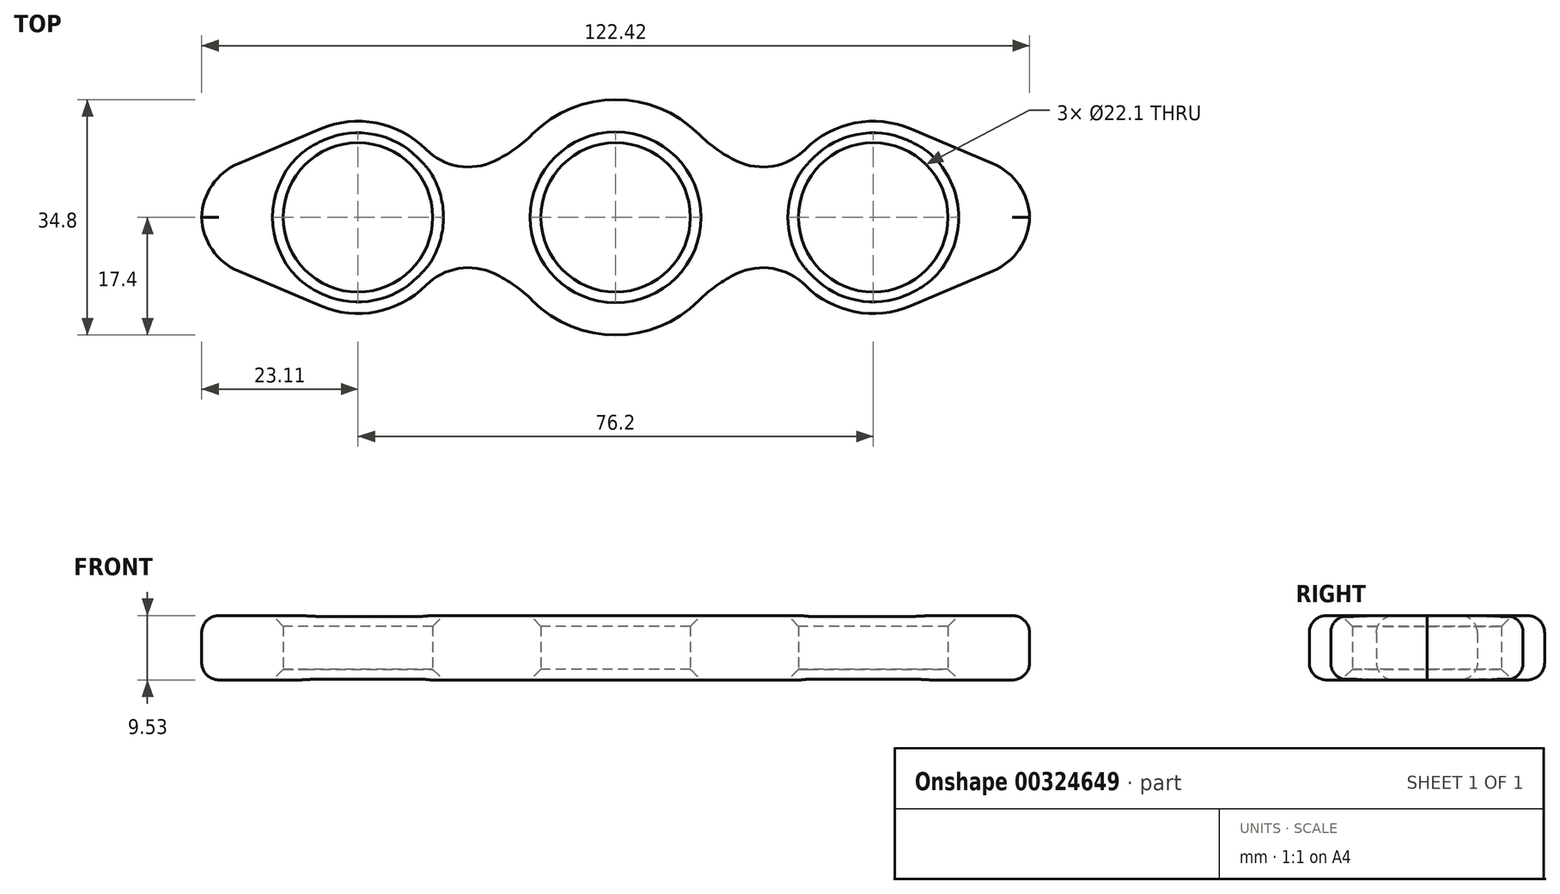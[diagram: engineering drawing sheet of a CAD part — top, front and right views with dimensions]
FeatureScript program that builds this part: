
annotation { "Feature Type Name" : "Feature", "Feature Type Description" : "" }
export const myFeature = defineFeature(function(context is Context, id is Id, definition is map)
    precondition{}
    {
        {
            var Q0;
            Q0=qCreatedBy(makeId("Top.planeOp"),FACE);
            var sketch = newSketch(context, id + "F0", { "sketchPlane" : qUnion([Q0])});
            skArc(sketch, "E0", {"start": v(0, 11.05) * mm, "mid": v(-7.81, 7.81) * mm, "end": v(-11.05, 0) * mm});
            skArc(sketch, "E1", {"start": v(-27.05, 0) * mm, "mid": v(-38.1, 11.05) * mm, "end": v(-49.15, 0) * mm});
            skArc(sketch, "E2", {"start": v(0, 17.4) * mm, "mid": v(-6.66, 16.07) * mm, "end": v(-12.3, 12.3) * mm});
            skArc(sketch, "E3", {"start": v(-28.04, 10.06) * mm, "mid": v(-35.39, 13.96) * mm, "end": v(-43.66, 13.1) * mm});
            skLineSegment(sketch, "E4", {"start": v(-43.66, 13.1) * mm, "end": v(-55.8, 7.94) * mm});
            skArc(sketch, "E5", {"start": v(-55.8, 7.94) * mm, "mid": v(-59.67, 4.77) * mm, "end": v(-61.2, 0) * mm});
            skPoint(sketch, "E6", {"position": v(0, 17.4) * mm});
            skArc(sketch, "E7", {"start": v(-17.9, 8.33) * mm, "mid": v(-14.94, 10.08) * mm, "end": v(-12.3, 12.3) * mm});
            skArc(sketch, "E8", {"start": v(-28.04, 10.06) * mm, "mid": v(-23.25, 7.58) * mm, "end": v(-17.9, 8.33) * mm});
            skLineSegment(sketch, "E9", {"start": v(0, 0) * mm, "end": v(-12.3, 12.3) * mm, "construction": true});
            skLineSegment(sketch, "E10", {"start": v(-38.1, 0) * mm, "end": v(-28.04, 10.06) * mm, "construction": true});
            skLineSegment(sketch, "E11", {"start": v(0, 17.4) * mm, "end": v(0, 0) * mm, "construction": true});
            skLineSegment(sketch, "E12", {"start": v(0, 0) * mm, "end": v(-61.2, 0) * mm, "construction": true});
            skPoint(sketch, "E13.center.orphan", {"position": v(38.1, 0) * mm});
            skPoint(sketch, "E14.end.orphan", {"position": v(-43.66, -13.1) * mm});
            skPoint(sketch, "E15.orphan", {"position": v(-55.8, -8.43) * mm});
            skArc(sketch, "E16.trimOffspring", {"start": v(-52.32, 0) * mm, "mid": v(-52.32, -0.12) * mm, "end": v(-52.32, -0.24) * mm});
            skArc(sketch, "E17.MirrorCS", {"start": v(-17.9, -8.33) * mm, "mid": v(-14.94, -10.08) * mm, "end": v(-12.3, -12.3) * mm});
            skArc(sketch, "E18.MirrorCS", {"start": v(-52.32, 0) * mm, "mid": v(-52.32, 0.12) * mm, "end": v(-52.32, 0.24) * mm});
            skLineSegment(sketch, "E19.MirrorCS", {"start": v(-43.66, -13.1) * mm, "end": v(-55.8, -7.94) * mm});
            skArc(sketch, "E20.MirrorCS", {"start": v(-55.8, -7.94) * mm, "mid": v(-59.67, -4.77) * mm, "end": v(-61.2, 0) * mm});
            skArc(sketch, "E21.MirrorCS", {"start": v(-28.04, -10.06) * mm, "mid": v(-23.25, -7.58) * mm, "end": v(-17.9, -8.33) * mm});
            skPoint(sketch, "E22.MirrorP", {"position": v(0, -17.4) * mm});
            skLineSegment(sketch, "E23.MirrorCS", {"start": v(0, 0) * mm, "end": v(-12.3, -12.3) * mm, "construction": true});
            skLineSegment(sketch, "E24.MirrorCS", {"start": v(0, -17.4) * mm, "end": v(0, 0) * mm, "construction": true});
            skArc(sketch, "E25.MirrorCS", {"start": v(-28.04, -10.06) * mm, "mid": v(-35.39, -13.96) * mm, "end": v(-43.66, -13.1) * mm});
            skArc(sketch, "E26.MirrorCS", {"start": v(-27.05, 0) * mm, "mid": v(-38.1, -11.05) * mm, "end": v(-49.15, 0) * mm});
            skArc(sketch, "E27.MirrorCS", {"start": v(0, -11.05) * mm, "mid": v(-7.81, -7.81) * mm, "end": v(-11.05, 0) * mm});
            skArc(sketch, "E28.MirrorCS", {"start": v(0, -17.4) * mm, "mid": v(-6.66, -16.07) * mm, "end": v(-12.3, -12.3) * mm});
            skLineSegment(sketch, "E29.MirrorCS", {"start": v(-38.1, 0) * mm, "end": v(-28.04, -10.06) * mm, "construction": true});
            skPoint(sketch, "E30.MirrorP", {"position": v(-55.8, 8.43) * mm});
            skArc(sketch, "E31.MirrorCS", {"start": v(52.32, 0) * mm, "mid": v(52.32, -0.12) * mm, "end": v(52.32, -0.24) * mm});
            skArc(sketch, "E32.MirrorCS", {"start": v(52.32, 0) * mm, "mid": v(52.32, 0.12) * mm, "end": v(52.32, 0.24) * mm});
            skArc(sketch, "E33.MirrorCS", {"start": v(17.9, 8.33) * mm, "mid": v(14.94, 10.08) * mm, "end": v(12.3, 12.3) * mm});
            skArc(sketch, "E34.MirrorCS", {"start": v(17.9, -8.33) * mm, "mid": v(14.94, -10.08) * mm, "end": v(12.3, -12.3) * mm});
            skPoint(sketch, "E35.MirrorP", {"position": v(55.8, 8.43) * mm});
            skArc(sketch, "E36.MirrorCS", {"start": v(55.8, -7.94) * mm, "mid": v(59.67, -4.77) * mm, "end": v(61.2, 0) * mm});
            skLineSegment(sketch, "E37.MirrorCS", {"start": v(0, 0) * mm, "end": v(12.3, -12.3) * mm, "construction": true});
            skPoint(sketch, "E38.MirrorP", {"position": v(43.66, -13.1) * mm});
            skArc(sketch, "E39.MirrorCS", {"start": v(28.04, -10.06) * mm, "mid": v(35.39, -13.96) * mm, "end": v(43.66, -13.1) * mm});
            skArc(sketch, "E40.MirrorCS", {"start": v(0, -11.05) * mm, "mid": v(7.81, -7.81) * mm, "end": v(11.05, 0) * mm});
            skArc(sketch, "E41.MirrorCS", {"start": v(0, -17.4) * mm, "mid": v(6.66, -16.07) * mm, "end": v(12.3, -12.3) * mm});
            skLineSegment(sketch, "E42.MirrorCS", {"start": v(0, 0) * mm, "end": v(61.2, 0) * mm, "construction": true});
            skLineSegment(sketch, "E43.MirrorCS", {"start": v(38.1, 0) * mm, "end": v(28.04, 10.06) * mm, "construction": true});
            skLineSegment(sketch, "E44.MirrorCS", {"start": v(0, 0) * mm, "end": v(12.3, 12.3) * mm, "construction": true});
            skArc(sketch, "E45.MirrorCS", {"start": v(28.04, 10.06) * mm, "mid": v(23.25, 7.58) * mm, "end": v(17.9, 8.33) * mm});
            skArc(sketch, "E46.MirrorCS", {"start": v(55.8, 7.94) * mm, "mid": v(59.67, 4.77) * mm, "end": v(61.2, 0) * mm});
            skLineSegment(sketch, "E47.MirrorCS", {"start": v(43.66, 13.1) * mm, "end": v(55.8, 7.94) * mm});
            skArc(sketch, "E48.MirrorCS", {"start": v(28.04, 10.06) * mm, "mid": v(35.39, 13.96) * mm, "end": v(43.66, 13.1) * mm});
            skArc(sketch, "E49.MirrorCS", {"start": v(0, 17.4) * mm, "mid": v(6.66, 16.07) * mm, "end": v(12.3, 12.3) * mm});
            skLineSegment(sketch, "E50.MirrorCS", {"start": v(38.1, 0) * mm, "end": v(28.04, -10.06) * mm, "construction": true});
            skArc(sketch, "E51.MirrorCS", {"start": v(27.05, 0) * mm, "mid": v(38.1, 11.05) * mm, "end": v(49.15, 0) * mm});
            skPoint(sketch, "E52.MirrorP", {"position": v(55.8, -8.43) * mm});
            skArc(sketch, "E53.MirrorCS", {"start": v(27.05, 0) * mm, "mid": v(38.1, -11.05) * mm, "end": v(49.15, 0) * mm});
            skArc(sketch, "E54.MirrorCS", {"start": v(28.04, -10.06) * mm, "mid": v(23.25, -7.58) * mm, "end": v(17.9, -8.33) * mm});
            skArc(sketch, "E55.MirrorCS", {"start": v(0, 11.05) * mm, "mid": v(7.81, 7.81) * mm, "end": v(11.05, 0) * mm});
            skLineSegment(sketch, "E56.MirrorCS", {"start": v(43.66, -13.1) * mm, "end": v(55.8, -7.94) * mm});
            skSolve(sketch);
        }
        {
            var Q0;
            Q0=makeQuery(id+"F0.imprint","IMPRINT",FACE,{"disambiguationData":[TD([[makeQuery(id+"F0.imprint","IMPRINT",EDGE,{"derivedFrom":sQuery(id+"F0.wireOp",EDGE,"E0")}),-1.0]])]});
            extrude(context, id + "F1", {"entities" : qUnion([Q0]), "depth" : 9.52 * mm});
        }
        {
            var Q0;
            Q0=makeQuery(id+"F1.opExtrude","CAP_EDGE",EDGE,{"disambiguationData":[OSD([sQuery(id+"F0.wireOp",EDGE,"E28.MirrorCS"),sQuery(id+"F0.wireOp",EDGE,"E41.MirrorCS")])],"isStart":false});
            var Q1;
            Q1=makeQuery(id+"F1.opExtrude","CAP_EDGE",EDGE,{"disambiguationData":[OSD([sQuery(id+"F0.wireOp",EDGE,"E17.MirrorCS")])],"isStart":false});
            var Q2;
            Q2=makeQuery(id+"F1.opExtrude","CAP_EDGE",EDGE,{"disambiguationData":[OSD([sQuery(id+"F0.wireOp",EDGE,"E21.MirrorCS")])],"isStart":false});
            var Q3;
            Q3=makeQuery(id+"F1.opExtrude","CAP_EDGE",EDGE,{"disambiguationData":[OSD([sQuery(id+"F0.wireOp",EDGE,"E25.MirrorCS")])],"isStart":false});
            var Q4;
            Q4=makeQuery(id+"F1.opExtrude","CAP_EDGE",EDGE,{"disambiguationData":[OSD([sQuery(id+"F0.wireOp",EDGE,"E19.MirrorCS")])],"isStart":false});
            var Q5;
            Q5=makeQuery(id+"F1.opExtrude","CAP_EDGE",EDGE,{"disambiguationData":[OSD([sQuery(id+"F0.wireOp",EDGE,"E20.MirrorCS")])],"isStart":false});
            var Q6;
            Q6=makeQuery(id+"F1.opExtrude","CAP_EDGE",EDGE,{"disambiguationData":[OSD([sQuery(id+"F0.wireOp",EDGE,"E5")])],"isStart":false});
            var Q7;
            Q7=makeQuery(id+"F1.opExtrude","CAP_EDGE",EDGE,{"disambiguationData":[OSD([sQuery(id+"F0.wireOp",EDGE,"E4")])],"isStart":false});
            var Q8;
            Q8=makeQuery(id+"F1.opExtrude","CAP_EDGE",EDGE,{"disambiguationData":[OSD([sQuery(id+"F0.wireOp",EDGE,"E28.MirrorCS"),sQuery(id+"F0.wireOp",EDGE,"E41.MirrorCS")])],"isStart":true});
            var Q9;
            Q9=makeQuery(id+"F1.opExtrude","CAP_EDGE",EDGE,{"disambiguationData":[OSD([sQuery(id+"F0.wireOp",EDGE,"E39.MirrorCS")])],"isStart":true});
            var Q10;
            Q10=makeQuery(id+"F1.opExtrude","CAP_EDGE",EDGE,{"disambiguationData":[OSD([sQuery(id+"F0.wireOp",EDGE,"E54.MirrorCS")])],"isStart":true});
            var Q11;
            Q11=makeQuery(id+"F1.opExtrude","CAP_EDGE",EDGE,{"disambiguationData":[OSD([sQuery(id+"F0.wireOp",EDGE,"E34.MirrorCS")])],"isStart":true});
            var Q12;
            Q12=makeQuery(id+"F1.opExtrude","CAP_EDGE",EDGE,{"disambiguationData":[OSD([sQuery(id+"F0.wireOp",EDGE,"E56.MirrorCS")])],"isStart":true});
            var Q13;
            Q13=makeQuery(id+"F1.opExtrude","CAP_EDGE",EDGE,{"disambiguationData":[OSD([sQuery(id+"F0.wireOp",EDGE,"E36.MirrorCS")])],"isStart":true});
            var Q14;
            Q14=makeQuery(id+"F1.opExtrude","CAP_EDGE",EDGE,{"disambiguationData":[OSD([sQuery(id+"F0.wireOp",EDGE,"E46.MirrorCS")])],"isStart":true});
            fillet(context, id + "F2", {"entities" : qUnion([Q0, Q1, Q2, Q3, Q4, Q5, Q6, Q7, Q8, Q9, Q10, Q11, Q12, Q13, Q14]), "radius" : 2.54 * mm, "tangentPropagation" : true, "allowEdgeOverflow" : false});
        }
        {
            var Q0;
            Q0=makeQuery(id+"F1.opExtrude","CAP_EDGE",EDGE,{"disambiguationData":[OSD([sQuery(id+"F0.wireOp",EDGE,"E0"),sQuery(id+"F0.wireOp",EDGE,"E27.MirrorCS"),sQuery(id+"F0.wireOp",EDGE,"E40.MirrorCS"),sQuery(id+"F0.wireOp",EDGE,"E55.MirrorCS")])],"isStart":false});
            var Q1;
            Q1=makeQuery(id+"F1.opExtrude","CAP_EDGE",EDGE,{"disambiguationData":[OSD([sQuery(id+"F0.wireOp",EDGE,"E0"),sQuery(id+"F0.wireOp",EDGE,"E27.MirrorCS"),sQuery(id+"F0.wireOp",EDGE,"E40.MirrorCS"),sQuery(id+"F0.wireOp",EDGE,"E55.MirrorCS")])],"isStart":true});
            var Q2;
            Q2=makeQuery(id+"F1.opExtrude","CAP_EDGE",EDGE,{"disambiguationData":[OSD([sQuery(id+"F0.wireOp",EDGE,"E1"),sQuery(id+"F0.wireOp",EDGE,"E26.MirrorCS")])],"isStart":false});
            var Q3;
            Q3=makeQuery(id+"F1.opExtrude","CAP_EDGE",EDGE,{"disambiguationData":[OSD([sQuery(id+"F0.wireOp",EDGE,"E1"),sQuery(id+"F0.wireOp",EDGE,"E26.MirrorCS")])],"isStart":true});
            var Q4;
            Q4=makeQuery(id+"F1.opExtrude","CAP_EDGE",EDGE,{"disambiguationData":[OSD([sQuery(id+"F0.wireOp",EDGE,"E51.MirrorCS"),sQuery(id+"F0.wireOp",EDGE,"E53.MirrorCS")])],"isStart":true});
            var Q5;
            Q5=makeQuery(id+"F1.opExtrude","CAP_EDGE",EDGE,{"disambiguationData":[OSD([sQuery(id+"F0.wireOp",EDGE,"E51.MirrorCS"),sQuery(id+"F0.wireOp",EDGE,"E53.MirrorCS")])],"isStart":false});
            chamfer(context, id + "F3", {"entities" : qUnion([Q0, Q1, Q2, Q3, Q4, Q5]), "width" : 1.59 * mm, "tangentPropagation" : true});
        }
    });
